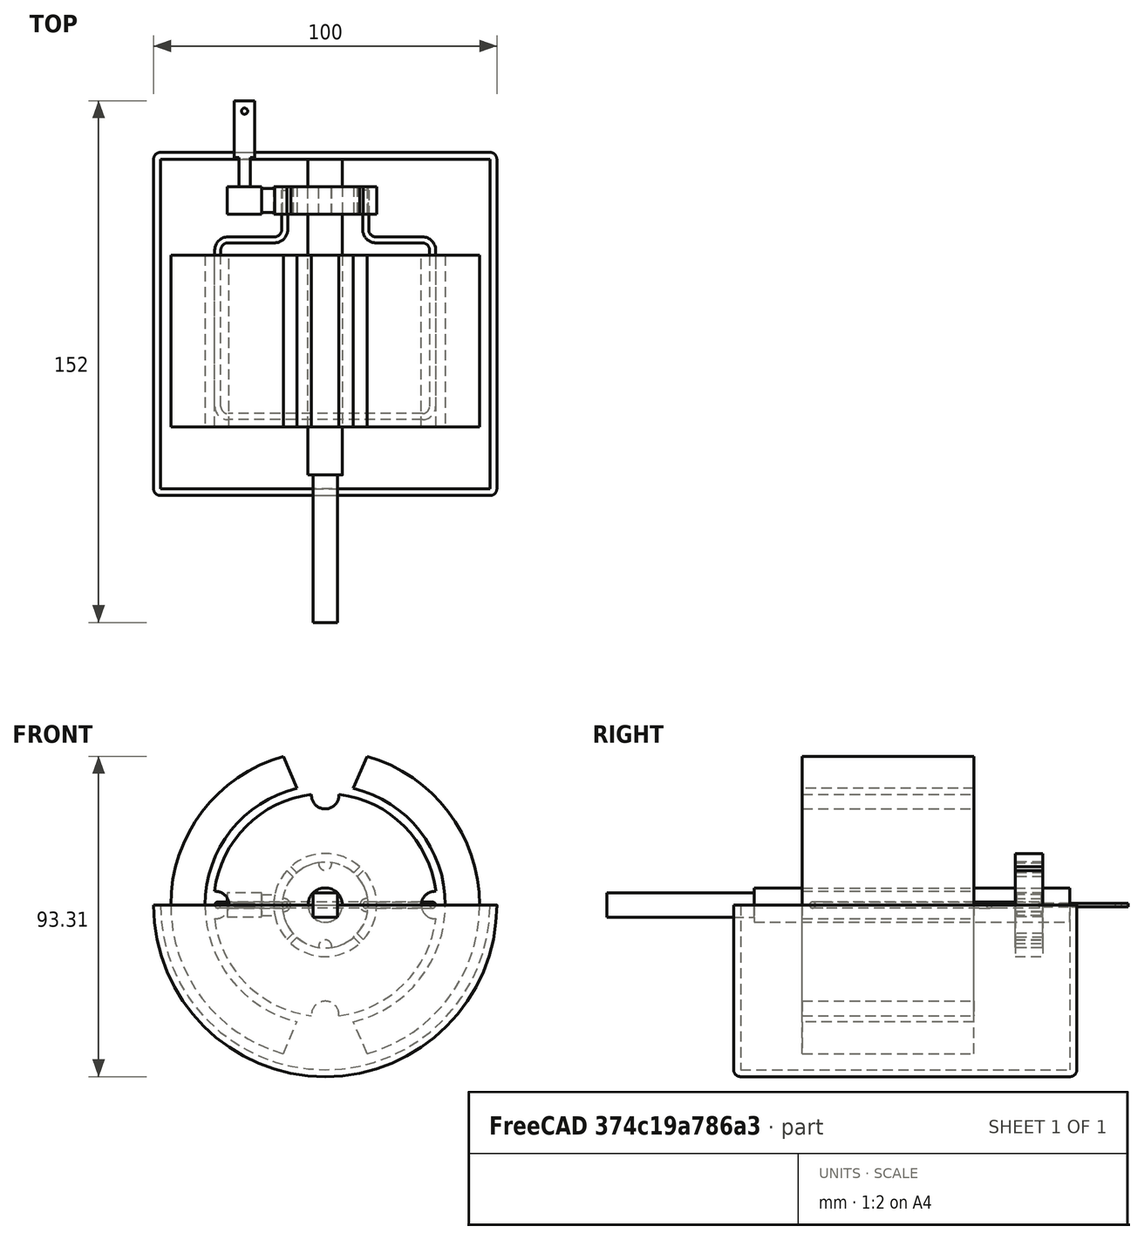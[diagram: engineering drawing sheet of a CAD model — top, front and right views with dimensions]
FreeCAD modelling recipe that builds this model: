
FCSTD DOCUMENT  (FreeCAD 1.0R39285 (Git))
Label: DCmotor
License: All rights reserved
LicenseURL: https://en.wikipedia.org/wiki/All_rights_reserved
objects: Sketcher::SketchObject×28, App::Link×15, PartDesign::Pocket×14, PartDesign::Pad×11, PartDesign::Body×10, PartDesign::Fillet×2, PartDesign::AdditivePipe×1, Spreadsheet::Sheet×1, App::DocumentObjectGroup×1, App::FeaturePython×1, Assembly::JointGroup×1, Assembly::AssemblyObject×1
note: 150 computed .brp shape members not serialized (recipe doc carries the construction recipe); baked Part::Feature solids carry a one-line shape summary decoded from their .brp

FEATURE [Sketcher::SketchObject] Sketch
  ArcFitTolerance = 1e-06
  AttachmentSupport = -> [XZ_Plane]
  FullyConstrained = true
  MakeInternals = false
  MapMode = 5
  Placement = pos=(0,0,0) rot=(1,0,0;1.5708rad)
  sketch-geometry (1):
    g0: Circle CenterX=0 CenterY=0 CenterZ=0 NormalX=0 NormalY=0 NormalZ=1 AngleXU=0 Radius=15
  constraints (2):
    c: Coincident(g0,g-1)
    c: Diameter(g0) = 30
FEATURE [PartDesign::Pad] Pad
  Direction = (0,-1,2e-16)
  Length = 8
  Length2 = 10
  Placement = pos=(0,0,0) rot=(1,0,0;1.5708rad)
  Profile = -> Sketch
  ReferenceAxis = -> Sketch [N_Axis]
  Refine = true
  Suppressed = false
  Type = 0
FEATURE [Sketcher::SketchObject] Sketch001
  ArcFitTolerance = 1e-06
  AttachmentSupport = -> [Pad]
  FullyConstrained = true
  MakeInternals = false
  MapMode = 5
  Placement = pos=(0,-8,0) rot=(1,0,0;1.5708rad)
  sketch-geometry (1):
    g0: Circle CenterX=0 CenterY=0 CenterZ=0 NormalX=0 NormalY=0 NormalZ=1 AngleXU=0 Radius=12.5
  constraints (2):
    c: Diameter(g0) = 25
    c: Coincident(g0,g-1)
FEATURE [PartDesign::Pocket] Pocket
  BaseFeature = -> Pad
  Direction = (0,1,-2e-16)
  Length = 5
  Length2 = 5
  Placement = pos=(0,0,0) rot=(1,0,0;1.5708rad)
  Profile = -> Sketch001
  ReferenceAxis = -> Sketch001 [N_Axis]
  Refine = true
  Suppressed = false
  Type = 1
FEATURE [Sketcher::SketchObject] Sketch002
  ArcFitTolerance = 1e-06
  AttachmentSupport = -> [Pocket]
  ExternalGeometry = -> [Pocket]
  FullyConstrained = true
  MakeInternals = false
  MapMode = 5
  Placement = pos=(0,-8,0) rot=(1,0,0;1.5708rad)
  sketch-geometry (8):
    g0: LineSegment StartX=-0.75 StartY=18.87 StartZ=0 EndX=-0.75 EndY=-18.87 EndZ=0
    g1: LineSegment StartX=-0.75 StartY=-18.87 StartZ=0 EndX=0.75 EndY=-18.87 EndZ=0
    g2: LineSegment StartX=0.75 StartY=-18.87 StartZ=0 EndX=0.75 EndY=18.87 EndZ=0
    g3: LineSegment StartX=0.75 StartY=18.87 StartZ=0 EndX=-0.75 EndY=18.87 EndZ=0
    g4: LineSegment StartX=-17.13 StartY=0.75 StartZ=0 EndX=-17.13 EndY=-0.75 EndZ=0
    g5: LineSegment StartX=-17.13 StartY=-0.75 StartZ=0 EndX=17.73 EndY=-0.75 EndZ=0
    g6: LineSegment StartX=17.73 StartY=-0.75 StartZ=0 EndX=17.73 EndY=0.75 EndZ=0
    g7: LineSegment StartX=17.73 StartY=0.75 StartZ=0 EndX=-17.13 EndY=0.75 EndZ=0
  constraints (21):
    c: Coincident(g0,g1)
    c: Coincident(g1,g2)
    c: Coincident(g2,g3)
    c: Coincident(g3,g0)
    c: Vertical(g0)
    c: Horizontal(g1)
    c: Symmetric(g0,g2,g-2)
    c: DistanceX(g0,g-1) = 0.75
    c: Coincident(g4,g5)
    c: Coincident(g5,g6)
    c: Coincident(g6,g7)
    c: Coincident(g7,g4)
    c: Vertical(g4)
    c: Horizontal(g5)
    c: Horizontal(g7)
    c: Symmetric(g5,g6,g-1)
    c: DistanceY(g5,g-1) = 0.75
    c: Symmetric(g1,g2,g-1)
    c: DistanceY(g1,g-1) = 18.87
    c: DistanceX(g4,g-1) = 17.13
    c: DistanceX(g-1,g5) = 17.73
FEATURE [PartDesign::Pocket] Pocket001
  BaseFeature = -> Pocket
  Direction = (0,1,-2e-16)
  Length = 5
  Length2 = 5
  Placement = pos=(0,0,0) rot=(1,0,0;1.5708rad)
  Profile = -> Sketch002
  ReferenceAxis = -> Sketch002 [N_Axis]
  Refine = true
  Suppressed = false
  Type = 1
FEATURE [PartDesign::Body] Body  label="Commutator"
  AllowCompound = true
  Group = -> [Sketch,Pad,Sketch001,Pocket,Sketch002,Pocket001]
  Origin = -> Origin
  Placement = pos=(0,15,1.08e-14) rot=(0,1,0;0.785398rad)
  Tip = -> Pocket001
FEATURE [Sketcher::SketchObject] Sketch003
  ArcFitTolerance = 1e-06
  AttachmentSupport = -> [XZ_Plane001]
  FullyConstrained = true
  MakeInternals = false
  MapMode = 5
  Placement = pos=(0,0,0) rot=(1,0,0;1.5708rad)
  sketch-geometry (1):
    g0: Circle CenterX=0 CenterY=0 CenterZ=0 NormalX=0 NormalY=0 NormalZ=1 AngleXU=0 Radius=45
  constraints (2):
    c: Coincident(g0,g-1)
    c: Diameter(g0) = 90
FEATURE [PartDesign::Pad] Pad001
  Direction = (0,-1,2e-16)
  Length = 50
  Length2 = 10
  Placement = pos=(0,0,0) rot=(1,0,0;1.5708rad)
  Profile = -> Sketch003
  ReferenceAxis = -> Sketch003 [N_Axis]
  Refine = true
  Suppressed = false
  Type = 0
FEATURE [Sketcher::SketchObject] Sketch004
  ArcFitTolerance = 1e-06
  AttachmentSupport = -> [Pad001]
  FullyConstrained = true
  MakeInternals = false
  MapMode = 5
  Placement = pos=(0,-50,0) rot=(1,0,0;1.5708rad)
  sketch-geometry (1):
    g0: Circle CenterX=0 CenterY=0 CenterZ=0 NormalX=0 NormalY=0 NormalZ=1 AngleXU=0 Radius=35
  constraints (2):
    c: Diameter(g0) = 70
    c: Coincident(g0,g-1)
FEATURE [PartDesign::Pocket] Pocket002
  BaseFeature = -> Pad001
  Direction = (0,1,-2e-16)
  Length = 5
  Length2 = 5
  Placement = pos=(0,0,0) rot=(1,0,0;1.5708rad)
  Profile = -> Sketch004
  ReferenceAxis = -> Sketch004 [N_Axis]
  Refine = true
  Suppressed = false
  Type = 1
FEATURE [Sketcher::SketchObject] Sketch005
  ArcFitTolerance = 1e-06
  AttachmentSupport = -> [Pocket002]
  ExternalGeometry = -> [Pocket002]
  FullyConstrained = true
  MakeInternals = false
  MapMode = 5
  Placement = pos=(0,-50,0) rot=(1,0,0;1.5708rad)
  sketch-geometry (8):
    g0: LineSegment StartX=-13 StartY=45.18 StartZ=0 EndX=13 EndY=45.18 EndZ=0
    g1: LineSegment StartX=-8.2 StartY=34 StartZ=0 EndX=8.2 EndY=34 EndZ=0
    g2: LineSegment StartX=-13 StartY=45.18 StartZ=0 EndX=-8.2 EndY=34 EndZ=0
    g3: LineSegment StartX=8.2 StartY=34 StartZ=0 EndX=13 EndY=45.18 EndZ=0
    g4: LineSegment StartX=-8.2 StartY=-34 StartZ=0 EndX=8.2 EndY=-34 EndZ=0
    g5: LineSegment StartX=8.2 StartY=-34 StartZ=0 EndX=13 EndY=-45.18 EndZ=0
    g6: LineSegment StartX=13 StartY=-45.18 StartZ=0 EndX=-13 EndY=-45.18 EndZ=0
    g7: LineSegment StartX=-13 StartY=-45.18 StartZ=0 EndX=-8.2 EndY=-34 EndZ=0
  constraints (20):
    c: DistanceX(g0,g-1) = 13
    c: Symmetric(g0,g0,g-2)
    c: Symmetric(g1,g1,g-2)
    c: DistanceX(g1,g-1) = 8.2
    c: Coincident(g2,g0)
    c: Coincident(g2,g1)
    c: Coincident(g3,g1)
    c: Coincident(g3,g0)
    c: DistanceY(g-1,g1) = 34
    c: DistanceY(g-1,g0) = 45.18
    c: Coincident(g4,g5)
    c: Coincident(g5,g6)
    c: Coincident(g6,g7)
    c: Coincident(g7,g4)
    c: Vertical(g4,g1)
    c: Symmetric(g4,g4,g-2)
    c: Symmetric(g6,g5,g-2)
    c: Vertical(g6,g0)
    c: Equal(g2,g7)
    c: DistanceY(g4,g-1) = 34
FEATURE [PartDesign::Pocket] Pocket003
  BaseFeature = -> Pocket002
  Direction = (0,1,-2e-16)
  Length = 5
  Length2 = 5
  Placement = pos=(0,0,0) rot=(1,0,0;1.5708rad)
  Profile = -> Sketch005
  ReferenceAxis = -> Sketch005 [N_Axis]
  Refine = true
  Suppressed = false
  Type = 1
FEATURE [PartDesign::Body] Body001  label="NorthMagnet"
  AllowCompound = false
  Group = -> [Sketch003,Pad001,Sketch004,Pocket002,Sketch005,Pocket003]
  Origin = -> Origin001
  Placement = pos=(0,-5,0) rot=(0,0,1;0rad)
  Tip = -> Pocket003
FEATURE [Sketcher::SketchObject] Sketch006
  ArcFitTolerance = 1e-06
  AttachmentSupport = -> [XZ_Plane002]
  FullyConstrained = true
  MakeInternals = false
  MapMode = 5
  Placement = pos=(0,0,0) rot=(1,0,0;1.5708rad)
  sketch-geometry (12):
    g0: LineSegment StartX=-18.57 StartY=3 StartZ=0 EndX=-18.57 EndY=-3 EndZ=0
    g1: LineSegment StartX=-18.57 StartY=-3 StartZ=0 EndX=-13.57 EndY=-3 EndZ=0
    g2: LineSegment StartX=-13.57 StartY=-3 StartZ=0 EndX=-13.57 EndY=3 EndZ=0
    g3: LineSegment StartX=-13.57 StartY=3 StartZ=0 EndX=-18.57 EndY=3 EndZ=0
    g4: LineSegment StartX=-28.57 StartY=3.5 StartZ=0 EndX=-28.57 EndY=-3.5 EndZ=0
    g5: LineSegment StartX=-28.57 StartY=-3.5 StartZ=0 EndX=-18.57 EndY=-3.5 EndZ=0
    g6: LineSegment StartX=-18.57 StartY=-3.5 StartZ=0 EndX=-18.57 EndY=3.5 EndZ=0
    g7: LineSegment StartX=-18.57 StartY=3.5 StartZ=0 EndX=-28.57 EndY=3.5 EndZ=0
    g8: LineSegment StartX=-31.07 StartY=0.75 StartZ=0 EndX=-31.07 EndY=-0.75 EndZ=0
    g9: LineSegment StartX=-31.07 StartY=-0.75 StartZ=0 EndX=-28.57 EndY=-0.75 EndZ=0
    g10: LineSegment StartX=-28.57 StartY=-0.75 StartZ=0 EndX=-28.57 EndY=0.75 EndZ=0
    g11: LineSegment StartX=-28.57 StartY=0.75 StartZ=0 EndX=-31.07 EndY=0.75 EndZ=0
  constraints (33):
    c: Coincident(g0,g1)
    c: Coincident(g1,g2)
    c: Coincident(g2,g3)
    c: Coincident(g3,g0)
    c: Vertical(g0)
    c: Horizontal(g1)
    c: Horizontal(g3)
    c: Symmetric(g1,g2,g-1)
    c: DistanceY(g-1,g2) = 3
    c: DistanceX(g0,g2) = 5
    c: DistanceX(g1,g-1) = 13.57
    c: Coincident(g4,g5)
    c: Coincident(g5,g6)
    c: Coincident(g6,g7)
    c: Coincident(g7,g4)
    c: Vertical(g4)
    c: Horizontal(g5)
    c: Horizontal(g7)
    c: Vertical(g6,g0)
    c: DistanceX(g4,g6) = 10
    c: DistanceY(g4,g4) = 7
    c: Symmetric(g5,g6,g-1)
    c: Coincident(g8,g9)
    c: Coincident(g9,g10)
    c: Coincident(g10,g11)
    c: Coincident(g11,g8)
    c: Vertical(g8)
    c: Horizontal(g9)
    c: Horizontal(g11)
    c: Vertical(g9,g4)
    c: Symmetric(g9,g10,g-1)
    c: DistanceY(g8,g8) = 1.5
    c: DistanceX(g8,g9) = 2.5
FEATURE [PartDesign::Pad] Pad002
  Direction = (0,-1,2e-16)
  Length = 8
  Length2 = 10
  Placement = pos=(0,0,0) rot=(1,0,0;1.5708rad)
  Profile = -> Sketch006
  ReferenceAxis = -> Sketch006 [N_Axis]
  Refine = true
  Suppressed = false
  Type = 0
FEATURE [Sketcher::SketchObject] Sketch007
  ArcFitTolerance = 1e-06
  AttachmentSupport = -> [Pad002]
  FullyConstrained = true
  MakeInternals = false
  MapMode = 5
  Placement = pos=(0,-8,4.2e-15) rot=(1,0,0;1.5708rad)
  sketch-geometry (1):
    g0: Circle CenterX=0 CenterY=0 CenterZ=0 NormalX=0 NormalY=0 NormalZ=1 AngleXU=0 Radius=15
  constraints (2):
    c: Diameter(g0) = 30
    c: Coincident(g0,g-1)
FEATURE [PartDesign::Pocket] Pocket004
  BaseFeature = -> Pad002
  Direction = (0,1,-2e-16)
  Length = 5
  Length2 = 5
  Placement = pos=(0,0,0) rot=(1,0,0;1.5708rad)
  Profile = -> Sketch007
  ReferenceAxis = -> Sketch007 [N_Axis]
  Refine = true
  Suppressed = false
  Type = 1
FEATURE [Sketcher::SketchObject] Sketch008
  ArcFitTolerance = 1e-06
  AttachmentSupport = -> [Pocket004]
  ExternalGeometry = -> [Pocket004]
  FullyConstrained = true
  MakeInternals = false
  MapMode = 5
  Placement = pos=(0,3e-16,0.75) rot=(0,0,1;3.14159rad)
  sketch-geometry (8):
    g0: LineSegment StartX=31.07 StartY=8 StartZ=0 EndX=28.57 EndY=8 EndZ=0
    g1: LineSegment StartX=28.57 StartY=8 StartZ=0 EndX=28.57 EndY=3.51 EndZ=0
    g2: LineSegment StartX=28.57 StartY=3.51 StartZ=0 EndX=31.07 EndY=3.51 EndZ=0
    g3: LineSegment StartX=31.07 StartY=3.51 StartZ=0 EndX=31.07 EndY=8 EndZ=0
    g4: LineSegment StartX=28.57 StartY=4.49 StartZ=0 EndX=28.57 EndY=0 EndZ=0
    g5: LineSegment StartX=28.57 StartY=0 StartZ=0 EndX=31.07 EndY=0 EndZ=0
    g6: LineSegment StartX=31.07 StartY=0 StartZ=0 EndX=31.07 EndY=4.49 EndZ=0
    g7: LineSegment StartX=31.07 StartY=4.49 StartZ=0 EndX=28.57 EndY=4.49 EndZ=0
  constraints (23):
    c: Coincident(g0,g1)
    c: Coincident(g1,g2)
    c: Coincident(g2,g3)
    c: Coincident(g3,g0)
    c: Horizontal(g0)
    c: Horizontal(g2)
    c: Vertical(g1)
    c: Vertical(g3)
    c: Coincident(g0,g-4)
    c: PointOnObject(g1,g-3)
    c: Coincident(g4,g5)
    c: Coincident(g5,g6)
    c: Coincident(g6,g7)
    c: Coincident(g7,g4)
    c: Vertical(g4)
    c: Vertical(g6)
    c: Horizontal(g5)
    c: Horizontal(g7)
    c: PointOnObject(g4,g-3)
    c: PointOnObject(g5,g-1)
    c: Vertical(g6,g2)
    c: Equal(g6,g3)
    c: DistanceY(g-1,g2) = 3.51
FEATURE [PartDesign::Pocket] Pocket005
  BaseFeature = -> Pocket004
  Direction = (0,0,-1)
  Length = 5
  Length2 = 5
  Placement = pos=(0,0,0) rot=(1,0,0;1.5708rad)
  Profile = -> Sketch008
  ReferenceAxis = -> Sketch008 [N_Axis]
  Refine = true
  Suppressed = false
  Type = 1
FEATURE [Sketcher::SketchObject] Sketch009
  ArcFitTolerance = 1e-06
  AttachmentSupport = -> [Pocket005]
  ExternalGeometry = -> [Pocket005]
  FullyConstrained = true
  MakeInternals = false
  MapMode = 5
  Placement = pos=(0,1.3e-15,3) rot=(0,0,1;3.14159rad)
  sketch-geometry (8):
    g0: LineSegment StartX=14.6969 StartY=8 StartZ=0 EndX=14.6969 EndY=7.5 EndZ=0
    g1: LineSegment StartX=14.6969 StartY=7.5 StartZ=0 EndX=18.57 EndY=7.5 EndZ=0
    g2: LineSegment StartX=18.57 StartY=7.5 StartZ=0 EndX=18.57 EndY=8 EndZ=0
    g3: LineSegment StartX=18.57 StartY=8 StartZ=0 EndX=14.6969 EndY=8 EndZ=0
    g4: LineSegment StartX=14.6969 StartY=0.5 StartZ=0 EndX=14.6969 EndY=-1e-16 EndZ=0
    g5: LineSegment StartX=14.6969 StartY=-1e-16 StartZ=0 EndX=18.57 EndY=-1e-16 EndZ=0
    g6: LineSegment StartX=18.57 StartY=-1e-16 StartZ=0 EndX=18.57 EndY=0.5 EndZ=0
    g7: LineSegment StartX=18.57 StartY=0.5 StartZ=0 EndX=14.6969 EndY=0.5 EndZ=0
  constraints (22):
    c: Coincident(g0,g1)
    c: Coincident(g1,g2)
    c: Coincident(g2,g3)
    c: Coincident(g3,g0)
    c: Vertical(g0)
    c: Vertical(g2)
    c: Horizontal(g1)
    c: Horizontal(g3)
    c: Coincident(g0,g-5)
    c: PointOnObject(g1,g-4)
    c: DistanceY(g1,g2) = 0.5
    c: Coincident(g4,g5)
    c: Coincident(g5,g6)
    c: Coincident(g6,g7)
    c: Coincident(g7,g4)
    c: Vertical(g4)
    c: Vertical(g6)
    c: Horizontal(g5)
    c: Horizontal(g7)
    c: PointOnObject(g4,g-5)
    c: Coincident(g5,g-4)
    c: DistanceY(g4,g4) = 0.5
FEATURE [PartDesign::Pocket] Pocket006
  BaseFeature = -> Pocket005
  Direction = (0,0,-1)
  Length = 5
  Length2 = 5
  Placement = pos=(0,0,0) rot=(1,0,0;1.5708rad)
  Profile = -> Sketch009
  ReferenceAxis = -> Sketch009 [N_Axis]
  Refine = true
  Suppressed = false
  Type = 1
FEATURE [PartDesign::Body] Body002  label="Brush"
  AllowCompound = false
  Group = -> [Sketch006,Pad002,Sketch007,Pocket004,Sketch008,Pocket005,Sketch009,Pocket006]
  Origin = -> Origin002
  Placement = pos=(0,15,0) rot=(0,0,1;0rad)
  Tip = -> Pocket006
FEATURE [Sketcher::SketchObject] Sketch010
  ArcFitTolerance = 1e-06
  AttachmentSupport = -> [XZ_Plane003]
  FullyConstrained = true
  MakeInternals = false
  MapMode = 5
  Placement = pos=(0,0,0) rot=(1,0,0;1.5708rad)
  sketch-geometry (1):
    g0: Circle CenterX=0 CenterY=0 CenterZ=0 NormalX=0 NormalY=0 NormalZ=1 AngleXU=0 Radius=45
  constraints (2):
    c: Coincident(g0,g-1)
    c: Diameter(g0) = 90
FEATURE [PartDesign::Pad] Pad003
  Direction = (0,-1,2e-16)
  Length = 50
  Length2 = 10
  Placement = pos=(0,0,0) rot=(1,0,0;1.5708rad)
  Profile = -> Sketch010
  ReferenceAxis = -> Sketch010 [N_Axis]
  Refine = true
  Suppressed = false
  Type = 0
FEATURE [Sketcher::SketchObject] Sketch011
  ArcFitTolerance = 1e-06
  AttachmentSupport = -> [Pad003]
  FullyConstrained = true
  MakeInternals = false
  MapMode = 5
  Placement = pos=(0,-50,0) rot=(1,0,0;1.5708rad)
  sketch-geometry (1):
    g0: Circle CenterX=0 CenterY=0 CenterZ=0 NormalX=0 NormalY=0 NormalZ=1 AngleXU=0 Radius=35
  constraints (2):
    c: Diameter(g0) = 70
    c: Coincident(g0,g-1)
FEATURE [PartDesign::Pocket] Pocket007
  BaseFeature = -> Pad003
  Direction = (0,1,-2e-16)
  Length = 5
  Length2 = 5
  Placement = pos=(0,0,0) rot=(1,0,0;1.5708rad)
  Profile = -> Sketch011
  ReferenceAxis = -> Sketch011 [N_Axis]
  Refine = true
  Suppressed = false
  Type = 1
FEATURE [Sketcher::SketchObject] Sketch012
  ArcFitTolerance = 1e-06
  AttachmentSupport = -> [Pocket007]
  ExternalGeometry = -> [Pocket007]
  FullyConstrained = true
  MakeInternals = false
  MapMode = 5
  Placement = pos=(0,-50,0) rot=(1,0,0;1.5708rad)
  sketch-geometry (8):
    g0: LineSegment StartX=-13 StartY=45.18 StartZ=0 EndX=13 EndY=45.18 EndZ=0
    g1: LineSegment StartX=-8.2 StartY=34 StartZ=0 EndX=8.2 EndY=34 EndZ=0
    g2: LineSegment StartX=-13 StartY=45.18 StartZ=0 EndX=-8.2 EndY=34 EndZ=0
    g3: LineSegment StartX=8.2 StartY=34 StartZ=0 EndX=13 EndY=45.18 EndZ=0
    g4: LineSegment StartX=-8.2 StartY=-34 StartZ=0 EndX=8.2 EndY=-34 EndZ=0
    g5: LineSegment StartX=8.2 StartY=-34 StartZ=0 EndX=13 EndY=-45.18 EndZ=0
    g6: LineSegment StartX=13 StartY=-45.18 StartZ=0 EndX=-13 EndY=-45.18 EndZ=0
    g7: LineSegment StartX=-13 StartY=-45.18 StartZ=0 EndX=-8.2 EndY=-34 EndZ=0
  constraints (20):
    c: DistanceX(g0,g-1) = 13
    c: Symmetric(g0,g0,g-2)
    c: Symmetric(g1,g1,g-2)
    c: DistanceX(g1,g-1) = 8.2
    c: Coincident(g2,g0)
    c: Coincident(g2,g1)
    c: Coincident(g3,g1)
    c: Coincident(g3,g0)
    c: DistanceY(g-1,g1) = 34
    c: DistanceY(g-1,g0) = 45.18
    c: Coincident(g4,g5)
    c: Coincident(g5,g6)
    c: Coincident(g6,g7)
    c: Coincident(g7,g4)
    c: Vertical(g4,g1)
    c: Symmetric(g4,g4,g-2)
    c: Symmetric(g6,g5,g-2)
    c: Vertical(g6,g0)
    c: Equal(g2,g7)
    c: DistanceY(g4,g-1) = 34
FEATURE [PartDesign::Pocket] Pocket008
  BaseFeature = -> Pocket007
  Direction = (0,1,-2e-16)
  Length = 5
  Length2 = 5
  Placement = pos=(0,0,0) rot=(1,0,0;1.5708rad)
  Profile = -> Sketch012
  ReferenceAxis = -> Sketch012 [N_Axis]
  Refine = true
  Suppressed = false
  Type = 1
FEATURE [PartDesign::Body] Body003  label="SouthMagnet"
  AllowCompound = false
  Group = -> [Sketch010,Pad003,Sketch011,Pocket007,Sketch012,Pocket008]
  Origin = -> Origin003
  Placement = pos=(0,-5,0) rot=(0,1,0;3.14159rad)
  Tip = -> Pocket008
FEATURE [Sketcher::SketchObject] Sketch013
  ArcFitTolerance = 1e-06
  AttachmentSupport = -> [XY_Plane004]
  FullyConstrained = true
  MakeInternals = false
  MapMode = 5
  sketch-geometry (19):
    g0: LineSegment StartX=11.8 StartY=11 StartZ=0 EndX=11.8 EndY=-0.5 EndZ=0
    g1: LineSegment StartX=14.8 StartY=-3.5 StartZ=0 EndX=28.3 EndY=-3.5 EndZ=0
    g2: LineSegment StartX=31.3 StartY=-6.5 StartZ=0 EndX=31.3 EndY=-52 EndZ=0
    g3: LineSegment StartX=28.3 StartY=-55 StartZ=0 EndX=-28.3 EndY=-55 EndZ=0
    g4: LineSegment StartX=-31.3 StartY=-52 StartZ=0 EndX=-31.3 EndY=-6.5 EndZ=0
    g5: LineSegment StartX=-28.3 StartY=-3.5 StartZ=0 EndX=-14.8 EndY=-3.5 EndZ=0
    g6: LineSegment StartX=-11.8 StartY=-0.5 StartZ=0 EndX=-11.8 EndY=11 EndZ=0
    g7: ArcOfCircle CenterX=28.3 CenterY=-6.5 CenterZ=0 NormalX=0 NormalY=0 NormalZ=1 AngleXU=0 Radius=3 StartAngle=0 EndAngle=1.5708
    g8: GeomPoint [constr] X=31.3 Y=-3.5 Z=0
    g9: ArcOfCircle CenterX=28.3 CenterY=-52 CenterZ=0 NormalX=0 NormalY=0 NormalZ=1 AngleXU=0 Radius=3 StartAngle=4.71239 EndAngle=6.28319
    g10: GeomPoint [constr] X=31.3 Y=-55 Z=0
    g11: ArcOfCircle CenterX=-28.3 CenterY=-6.5 CenterZ=0 NormalX=0 NormalY=0 NormalZ=1 AngleXU=0 Radius=3 StartAngle=1.5708 EndAngle=3.14159
    g12: GeomPoint [constr] X=-31.3 Y=-3.5 Z=0
    g13: ArcOfCircle CenterX=-28.3 CenterY=-52 CenterZ=0 NormalX=0 NormalY=0 NormalZ=1 AngleXU=0 Radius=3 StartAngle=3.14159 EndAngle=4.71239
    g14: GeomPoint [constr] X=-31.3 Y=-55 Z=0
    g15: ArcOfCircle CenterX=14.8 CenterY=-0.5 CenterZ=0 NormalX=0 NormalY=0 NormalZ=1 AngleXU=0 Radius=3 StartAngle=3.14159 EndAngle=4.71239
    g16: GeomPoint [constr] X=11.8 Y=-3.5 Z=0
    g17: ArcOfCircle CenterX=-14.8 CenterY=-0.5 CenterZ=0 NormalX=0 NormalY=0 NormalZ=1 AngleXU=0 Radius=3 StartAngle=4.71239 EndAngle=6.28319
    g18: GeomPoint [constr] X=-11.8 Y=-3.5 Z=0
  constraints (44):
    c: Vertical(g0)
    c: Horizontal(g1)
    c: Vertical(g2)
    c: Vertical(g4)
    c: Horizontal(g5)
    c: Vertical(g6)
    c: Symmetric(g6,g0,g-2)
    c: Horizontal(g16,g18)
    c: Symmetric(g10,g14,g-2)
    c: DistanceX(g6,g-1) = 11.8
    c: DistanceY(g-1,g6) = 11
    c: DistanceX(g12,g18) = 19.5
    c: DistanceY(g12,g-1) = 3.5
    c: DistanceY(g14,g-1) = 55
    c: PointOnObject(g8,g1)
    c: PointOnObject(g8,g2)
    c: Tangent(g1,g7) = 1.5708
    c: Tangent(g2,g7) = 1.5708
    c: DistanceX(g7,g2) = 3
    c: PointOnObject(g10,g2)
    c: PointOnObject(g10,g3)
    c: Tangent(g2,g9) = 1.5708
    c: Tangent(g3,g9) = 1.5708
    c: PointOnObject(g12,g4)
    c: PointOnObject(g12,g5)
    c: Tangent(g4,g11) = 1.5708
    c: Tangent(g5,g11) = 1.5708
    c: PointOnObject(g14,g3)
    c: PointOnObject(g14,g4)
    c: Tangent(g3,g13) = 1.5708
    c: Tangent(g4,g13) = 1.5708
    c: Vertical(g1,g3)
    c: Horizontal(g2,g4)
    c: Vertical(g3,g5)
    c: PointOnObject(g16,g0)
    c: PointOnObject(g16,g1)
    c: Tangent(g0,g15) = -1.5708
    c: Tangent(g1,g15) = -1.5708
    c: PointOnObject(g18,g5)
    c: PointOnObject(g18,g6)
    c: Tangent(g5,g17) = -1.5708
    c: Tangent(g6,g17) = -1.5708
    c: Equal(g11,g17)
    c: Equal(g17,g15)
FEATURE [Sketcher::SketchObject] Sketch014
  ArcFitTolerance = 1e-06
  AttachmentSupport = -> [XZ_Plane004]
  FullyConstrained = true
  MakeInternals = false
  MapMode = 5
  Placement = pos=(0,0,0) rot=(1,0,0;1.5708rad)
  sketch-geometry (1):
    g0: Circle CenterX=11.8 CenterY=0 CenterZ=0 NormalX=0 NormalY=0 NormalZ=1 AngleXU=0 Radius=0.875
  constraints (3):
    c: Diameter(g0) = 1.75
    c: PointOnObject(g0,g-1)
    c: DistanceX(g-1,g0) = 11.8
FEATURE [PartDesign::AdditivePipe] AdditivePipe
  AuxilleryCurvelinear = true
  AuxillerySpineTangent = false
  Binormal = (0,0,0)
  Mode = 0
  Placement = pos=(0,0,0) rot=(1,0,0;1.5708rad)
  Profile = -> Sketch014
  Refine = true
  Spine = -> Sketch013
  SpineTangent = false
  Suppressed = false
  Transformation = 0
  Transition = 0
FEATURE [PartDesign::Body] Body004  label="Rotor"
  AllowCompound = false
  Group = -> [Sketch013,Sketch014,AdditivePipe]
  Origin = -> Origin004
  Placement = pos=(0,3,0) rot=(0,1,0;0rad)
  Tip = -> AdditivePipe
FEATURE [Sketcher::SketchObject] Sketch015
  ArcFitTolerance = 1e-06
  AttachmentSupport = -> [XZ_Plane006]
  FullyConstrained = true
  MakeInternals = false
  MapMode = 5
  Placement = pos=(0,0,0) rot=(1,0,0;1.5708rad)
  sketch-geometry (1):
    g0: Circle CenterX=0 CenterY=0 CenterZ=0 NormalX=0 NormalY=0 NormalZ=1 AngleXU=0 Radius=5
  constraints (2):
    c: Coincident(g0,g-1)
    c: Diameter(g0) = 10
FEATURE [PartDesign::Pad] Pad004
  Direction = (0,-1,2e-16)
  Length = 135
  Length2 = 10
  Placement = pos=(0,0,0) rot=(1,0,0;1.5708rad)
  Profile = -> Sketch015 [Edge1]
  ReferenceAxis = -> Sketch015 [N_Axis]
  Refine = true
  Suppressed = false
  Type = 0
FEATURE [Sketcher::SketchObject] Sketch016
  ArcFitTolerance = 1e-06
  AttachmentSupport = -> [XY_Plane007]
  FullyConstrained = true
  MakeInternals = false
  MapMode = 5
  sketch-geometry (9):
    g0: LineSegment StartX=-25.16 StartY=15 StartZ=0 EndX=-25.16 EndY=23.5 EndZ=0
    g1: LineSegment StartX=-25.16 StartY=23.5 StartZ=0 EndX=-26.49 EndY=23.5 EndZ=0
    g2: LineSegment StartX=-26.49 StartY=23.5 StartZ=0 EndX=-26.49 EndY=40 EndZ=0
    g3: LineSegment StartX=-26.49 StartY=40 StartZ=0 EndX=-20.5 EndY=40 EndZ=0
    g4: LineSegment StartX=-20.5 StartY=40 StartZ=0 EndX=-20.5 EndY=23.5 EndZ=0
    g5: LineSegment StartX=-20.5 StartY=23.5 StartZ=0 EndX=-21.83 EndY=23.5 EndZ=0
    g6: LineSegment StartX=-21.83 StartY=23.5 StartZ=0 EndX=-21.83 EndY=15 EndZ=0
    g7: LineSegment StartX=-21.83 StartY=15 StartZ=0 EndX=-25.16 EndY=15 EndZ=0
    g8: Circle CenterX=-23.5 CenterY=37 CenterZ=0 NormalX=0 NormalY=0 NormalZ=1 AngleXU=0 Radius=0.9
  constraints (27):
    c: Vertical(g0)
    c: Coincident(g0,g1)
    c: Coincident(g1,g2)
    c: Vertical(g2)
    c: Coincident(g2,g3)
    c: Horizontal(g3)
    c: Coincident(g3,g4)
    c: Vertical(g4)
    c: Coincident(g4,g5)
    c: Horizontal(g5)
    c: Coincident(g5,g6)
    c: Vertical(g6)
    c: Coincident(g6,g7)
    c: Coincident(g7,g0)
    c: Horizontal(g7)
    c: DistanceY(g-1,g0) = 15
    c: Horizontal(g1,g0)
    c: Horizontal(g5,g0)
    c: DistanceX(g6,g-1) = 21.83
    c: DistanceX(g0,g-1) = 25.16
    c: DistanceX(g4,g-1) = 20.5
    c: Equal(g5,g1)
    c: DistanceY(g-1,g4) = 23.5
    c: DistanceY(g-1,g2) = 40
    c: DistanceX(g8,g-1) = 23.5
    c: Diameter(g8) = 1.8
    c: DistanceY(g-1,g8) = 37
FEATURE [PartDesign::Pad] Pad005
  Direction = (0,0,1)
  Length = 1
  Length2 = 10
  Profile = -> Sketch016
  ReferenceAxis = -> Sketch016 [N_Axis]
  Refine = true
  Suppressed = false
  Type = 0
FEATURE [PartDesign::Body] Body006  label="BrushArms"
  AllowCompound = false
  Group = -> [Sketch016,Pad005]
  Origin = -> Origin007
  Placement = pos=(0,0,-0.5) rot=(0,0,1;0rad)
  Tip = -> Pad005
FEATURE [Sketcher::SketchObject] Sketch017
  ArcFitTolerance = 1e-06
  AttachmentSupport = -> [XZ_Plane008]
  FullyConstrained = true
  MakeInternals = false
  MapMode = 5
  Placement = pos=(0,0,0) rot=(1,0,0;1.5708rad)
  sketch-geometry (1):
    g0: Circle CenterX=0 CenterY=0 CenterZ=0 NormalX=0 NormalY=0 NormalZ=1 AngleXU=0 Radius=12.5
  constraints (2):
    c: Diameter(g0) = 25
    c: Coincident(g0,g-1)
FEATURE [PartDesign::Pad] Pad006
  Direction = (0,-1,2e-16)
  Length = 8
  Length2 = 10
  Placement = pos=(0,0,0) rot=(1,0,0;1.5708rad)
  Profile = -> Sketch017
  ReferenceAxis = -> Sketch017 [N_Axis]
  Refine = true
  Suppressed = false
  Type = 0
FEATURE [Sketcher::SketchObject] Sketch018
  ArcFitTolerance = 1e-06
  AttachmentSupport = -> [XZ_Plane008]
  FullyConstrained = true
  MakeInternals = false
  MapMode = 5
  Placement = pos=(0,0,0) rot=(1,0,0;1.5708rad)
  sketch-geometry (4):
    g0: Circle CenterX=12 CenterY=0 CenterZ=0 NormalX=0 NormalY=0 NormalZ=1 AngleXU=0 Radius=1.875
    g1: Circle CenterX=-12 CenterY=0 CenterZ=0 NormalX=0 NormalY=0 NormalZ=1 AngleXU=0 Radius=1.875
    g2: Circle CenterX=0 CenterY=12 CenterZ=0 NormalX=0 NormalY=0 NormalZ=1 AngleXU=0 Radius=1.875
    g3: Circle CenterX=0 CenterY=-12 CenterZ=0 NormalX=0 NormalY=0 NormalZ=1 AngleXU=0 Radius=1.875
  constraints (10):
    c: Diameter(g0) = 3.75
    c: PointOnObject(g0,g-1)
    c: DistanceX(g-1,g0) = 12
    c: Symmetric(g1,g0,g-2)
    c: Equal(g1,g0)
    c: PointOnObject(g2,g-2)
    c: Equal(g2,g1)
    c: DistanceY(g-1,g2) = 12
    c: Equal(g3,g1)
    c: Symmetric(g3,g2,g-1)
FEATURE [PartDesign::Pocket] Pocket009
  BaseFeature = -> Pad006
  Direction = (0,1,-2e-16)
  Length = 5
  Length2 = 5
  Placement = pos=(0,0,0) rot=(1,0,0;1.5708rad)
  Profile = -> Sketch018
  ReferenceAxis = -> Sketch018 [N_Axis]
  Refine = true
  Reversed = true
  Suppressed = false
  Type = 1
FEATURE [PartDesign::Body] Body007  label="CommutatorSupport"
  AllowCompound = false
  Group = -> [Sketch017,Pad006,Sketch018,Pocket009]
  Origin = -> Origin008
  Placement = pos=(0,15,0) rot=(0,1,0;0rad)
  Tip = -> Pocket009
FEATURE [Sketcher::SketchObject] Sketch019
  ArcFitTolerance = 1e-06
  AttachmentSupport = -> [XZ_Plane009]
  FullyConstrained = true
  MakeInternals = false
  MapMode = 5
  Placement = pos=(0,0,0) rot=(1,0,0;1.5708rad)
  sketch-geometry (1):
    g0: Circle CenterX=0 CenterY=0 CenterZ=0 NormalX=0 NormalY=0 NormalZ=1 AngleXU=0 Radius=32.5
  constraints (2):
    c: Diameter(g0) = 65
    c: Coincident(g0,g-1)
FEATURE [PartDesign::Pad] Pad007
  Direction = (0,-1,2e-16)
  Length = 50
  Length2 = 10
  Placement = pos=(0,0,0) rot=(1,0,0;1.5708rad)
  Profile = -> Sketch019
  ReferenceAxis = -> Sketch019 [N_Axis]
  Refine = true
  Suppressed = false
  Type = 0
FEATURE [Sketcher::SketchObject] Sketch020
  ArcFitTolerance = 1e-06
  AttachmentSupport = -> [Pad007]
  FullyConstrained = true
  MakeInternals = false
  MapMode = 5
  Placement = pos=(0,0,0) rot=(-1,0,0;1.5708rad)
  sketch-geometry (4):
    g0: Circle CenterX=32 CenterY=0 CenterZ=0 NormalX=0 NormalY=0 NormalZ=1 AngleXU=0 Radius=4
    g1: Circle CenterX=-32 CenterY=0 CenterZ=0 NormalX=0 NormalY=0 NormalZ=1 AngleXU=0 Radius=4
    g2: Circle CenterX=0 CenterY=-32 CenterZ=0 NormalX=0 NormalY=0 NormalZ=1 AngleXU=0 Radius=4
    g3: Circle CenterX=-2e-16 CenterY=32 CenterZ=0 NormalX=0 NormalY=0 NormalZ=1 AngleXU=0 Radius=4
  constraints (10):
    c: PointOnObject(g0,g-1)
    c: Diameter(g0) = 8
    c: DistanceX(g-1,g0) = 32
    c: Symmetric(g1,g0,g-2)
    c: Equal(g1,g0)
    c: PointOnObject(g2,g-2)
    c: DistanceY(g2,g-1) = 32
    c: Symmetric(g3,g2,g-1)
    c: Equal(g0,g2)
    c: Equal(g3,g0)
FEATURE [PartDesign::Pocket] Pocket010
  BaseFeature = -> Pad007
  Direction = (0,-1,-2e-16)
  Length = 5
  Length2 = 5
  Placement = pos=(0,0,0) rot=(1,0,0;1.5708rad)
  Profile = -> Sketch020
  ReferenceAxis = -> Sketch020 [N_Axis]
  Refine = true
  Suppressed = false
  Type = 1
FEATURE [PartDesign::Body] Body008  label="RotorSupport"
  AllowCompound = false
  Group = -> [Sketch019,Pad007,Sketch020,Pocket010]
  Origin = -> Origin009
  Placement = pos=(0,-5,0) rot=(0,1,0;0rad)
  Tip = -> Pocket010
FEATURE [Sketcher::SketchObject] Sketch021
  ArcFitTolerance = 1e-06
  AttachmentSupport = -> [XZ_Plane010]
  FullyConstrained = true
  MakeInternals = false
  MapMode = 5
  Placement = pos=(0,0,0) rot=(1,0,0;1.5708rad)
  sketch-geometry (2):
    g0: ArcOfCircle CenterX=0 CenterY=0 CenterZ=0 NormalX=0 NormalY=0 NormalZ=1 AngleXU=0 Radius=50 StartAngle=3.14159 EndAngle=6.28319
    g1: LineSegment StartX=50 StartY=-1.22e-14 StartZ=0 EndX=-50 EndY=1.73205e-05 EndZ=0
  constraints (6):
    c: Angle(g0) = 3.14159
    c: Coincident(g0,g-1)
    c: PointOnObject(g0,g-1)
    c: DistanceX(g-1,g0) = 50
    c: Coincident(g1,g0)
    c: Coincident(g1,g0)
FEATURE [PartDesign::Pad] Pad008
  Direction = (0,-1,2e-16)
  Length = 100
  Length2 = 10
  Placement = pos=(0,0,0) rot=(1,0,0;1.5708rad)
  Profile = -> Sketch021
  ReferenceAxis = -> Sketch021 [N_Axis]
  Refine = true
  Suppressed = false
  Type = 0
FEATURE [Sketcher::SketchObject] Sketch022
  ArcFitTolerance = 1e-06
  AttachmentSupport = -> [XZ_Plane010]
  FullyConstrained = true
  MakeInternals = false
  MapMode = 5
  Placement = pos=(0,0,0) rot=(1,0,0;1.5708rad)
  sketch-geometry (2):
    g0: ArcOfCircle CenterX=0 CenterY=0 CenterZ=0 NormalX=0 NormalY=0 NormalZ=1 AngleXU=0 Radius=48 StartAngle=3.14159 EndAngle=6.28319
    g1: LineSegment StartX=48 StartY=0 StartZ=0 EndX=-48 EndY=5.9e-15 EndZ=0
  constraints (6):
    c: Radius(g0) = 48
    c: Coincident(g0,g-1)
    c: PointOnObject(g0,g-1)
    c: PointOnObject(g0,g-1)
    c: Coincident(g1,g0)
    c: Coincident(g1,g0)
FEATURE [PartDesign::Pocket] Pocket011
  BaseFeature = -> Pad008
  Direction = (0,1,-2e-16)
  Length = 5
  Length2 = 5
  Placement = pos=(0,0,0) rot=(1,0,0;1.5708rad)
  Profile = -> Sketch022
  ReferenceAxis = -> Sketch022 [N_Axis]
  Refine = true
  Reversed = true
  Suppressed = false
  Type = 1
FEATURE [Sketcher::SketchObject] Sketch023
  ArcFitTolerance = 1e-06
  AttachmentSupport = -> [XZ_Plane010]
  FullyConstrained = true
  MakeInternals = false
  MapMode = 5
  Placement = pos=(0,0,0) rot=(1,0,0;1.5708rad)
  sketch-geometry (2):
    g0: ArcOfCircle CenterX=0 CenterY=0 CenterZ=0 NormalX=0 NormalY=0 NormalZ=1 AngleXU=0 Radius=48.02 StartAngle=3.14159 EndAngle=6.28319
    g1: LineSegment StartX=-48.02 StartY=0 StartZ=0 EndX=48.02 EndY=0 EndZ=0
  constraints (6):
    c: Radius(g0) = 48.02
    c: Coincident(g0,g-1)
    c: PointOnObject(g0,g-1)
    c: PointOnObject(g0,g-1)
    c: Coincident(g1,g0)
    c: Coincident(g1,g0)
FEATURE [PartDesign::Pad] Pad009
  BaseFeature = -> Pocket011
  Direction = (0,-1,2e-16)
  Length = 2
  Length2 = 10
  Placement = pos=(0,0,0) rot=(1,0,0;1.5708rad)
  Profile = -> Sketch023
  ReferenceAxis = -> Sketch023 [N_Axis]
  Refine = true
  Suppressed = false
  Type = 0
FEATURE [Sketcher::SketchObject] Sketch024
  ArcFitTolerance = 1e-06
  AttachmentSupport = -> [Pad009]
  FullyConstrained = true
  MakeInternals = false
  MapMode = 5
  Placement = pos=(0,-100,2.2e-14) rot=(1,0,0;1.5708rad)
  sketch-geometry (2):
    g0: ArcOfCircle CenterX=0 CenterY=0 CenterZ=0 NormalX=0 NormalY=0 NormalZ=1 AngleXU=0 Radius=48.02 StartAngle=3.14159 EndAngle=6.28319
    g1: LineSegment StartX=-48.02 StartY=5.9e-15 StartZ=0 EndX=48.02 EndY=0 EndZ=0
  constraints (6):
    c: Radius(g0) = 48.02
    c: Coincident(g0,g-1)
    c: PointOnObject(g0,g-1)
    c: PointOnObject(g0,g-1)
    c: Coincident(g1,g0)
    c: Coincident(g1,g0)
FEATURE [PartDesign::Pad] Pad010
  BaseFeature = -> Pad009
  Direction = (0,-1,2e-16)
  Length = 2
  Length2 = 10
  Placement = pos=(0,0,0) rot=(1,0,0;1.5708rad)
  Profile = -> Sketch024
  ReferenceAxis = -> Sketch024 [N_Axis]
  Refine = true
  Reversed = true
  Suppressed = false
  Type = 0
FEATURE [PartDesign::Fillet] Fillet
  Base = -> Pad010 [Edge8]
  BaseFeature = -> Pad010
  Placement = pos=(0,0,0) rot=(1,0,0;1.5708rad)
  Radius = 2
  Refine = true
  SupportTransform = false
  Suppressed = false
  UseAllEdges = false
FEATURE [PartDesign::Fillet] Fillet001
  Base = -> Fillet [Edge3]
  BaseFeature = -> Fillet
  Placement = pos=(0,0,0) rot=(1,0,0;1.5708rad)
  Radius = 2
  Refine = true
  SupportTransform = false
  Suppressed = false
  UseAllEdges = false
FEATURE [Sketcher::SketchObject] Sketch025
  ArcFitTolerance = 1e-06
  AttachmentSupport = -> [XZ_Plane010]
  FullyConstrained = true
  MakeInternals = false
  MapMode = 5
  Placement = pos=(0,0,0) rot=(1,0,0;1.5708rad)
FEATURE [PartDesign::Body] Body009  label="Case"
  AllowCompound = false
  Group = -> [Sketch021,Pad008,Sketch022,Pocket011,Sketch023,Pad009,Sketch024,Pad010,Fillet,Fillet001,Sketch025]
  Origin = -> Origin010
  Placement = pos=(0,25,0) rot=(0,0,1;0rad)
  Tip = -> Fillet001
FEATURE [Sketcher::SketchObject] Sketch026
  ArcFitTolerance = 1e-06
  AttachmentSupport = -> [Pad004]
  ExternalGeometry = -> [Pad004]
  FullyConstrained = true
  MakeInternals = false
  MapMode = 5
  Placement = pos=(0,-135,0) rot=(1,0,0;1.5708rad)
  sketch-geometry (6):
    g0: LineSegment StartX=3.53106 StartY=-3.54 StartZ=0 EndX=3.53106 EndY=3.54 EndZ=0
    g1: LineSegment StartX=3.53106 StartY=3.54 StartZ=0 EndX=-3.53106 EndY=3.54 EndZ=0
    g2: LineSegment StartX=-3.53106 StartY=3.54 StartZ=0 EndX=-3.87 EndY=6.02 EndZ=0
    g3: LineSegment StartX=-3.87 StartY=6.02 StartZ=0 EndX=6.78 EndY=6.02 EndZ=0
    g4: LineSegment StartX=6.78 StartY=6.02 StartZ=0 EndX=6.88 EndY=-3.72 EndZ=0
    g5: LineSegment StartX=6.88 StartY=-3.72 StartZ=0 EndX=3.53106 EndY=-3.54 EndZ=0
  constraints (18):
    c: Coincident(g0,g1)
    c: Vertical(g0)
    c: Horizontal(g1)
    c: PointOnObject(g1,g-3)
    c: PointOnObject(g0,g-3)
    c: Coincident(g1,g2)
    c: Coincident(g2,g3)
    c: Horizontal(g3)
    c: Coincident(g3,g4)
    c: Coincident(g4,g5)
    c: Coincident(g5,g0)
    c: DistanceY(g1,g2) = 2.48
    c: DistanceX(g2,g3) = 10.65
    c: DistanceY(g4,g3) = 9.74
    c: DistanceY(g4,g-1) = 3.72
    c: DistanceX(g-1,g3) = 6.78
    c: PointOnObject(g0,g-3)
    c: DistanceX(g-1,g4) = 6.88
FEATURE [PartDesign::Pocket] Pocket012
  BaseFeature = -> Pad004
  Direction = (0,1,-2e-16)
  Length = 43
  Length2 = 5
  Placement = pos=(0,0,0) rot=(1,0,0;1.5708rad)
  Profile = -> Sketch026
  ReferenceAxis = -> Sketch026 [N_Axis]
  Refine = true
  Suppressed = false
  Type = 0
FEATURE [Sketcher::SketchObject] Sketch027
  ArcFitTolerance = 1e-06
  AttachmentSupport = -> [Pocket012]
  ExternalGeometry = -> [Pocket012]
  FullyConstrained = true
  MakeInternals = false
  MapMode = 5
  Placement = pos=(0,-135,0) rot=(1,0,0;1.5708rad)
  sketch-geometry (6):
    g0: LineSegment StartX=-3.53106 StartY=3.54 StartZ=0 EndX=-3.53106 EndY=-3.54 EndZ=0
    g1: LineSegment StartX=-3.53106 StartY=-3.54 StartZ=0 EndX=3.53106 EndY=-3.54 EndZ=0
    g2: LineSegment StartX=-3.53106 StartY=3.54 StartZ=0 EndX=-6.79 EndY=3.54 EndZ=0
    g3: LineSegment StartX=-6.79 StartY=3.54 StartZ=0 EndX=-6.79 EndY=-6.25 EndZ=0
    g4: LineSegment StartX=-6.79 StartY=-6.25 StartZ=0 EndX=3.53106 EndY=-6.25 EndZ=0
    g5: LineSegment StartX=3.53106 StartY=-6.25 StartZ=0 EndX=3.53106 EndY=-3.54 EndZ=0
  constraints (16):
    c: Coincident(g-5,g0)
    c: PointOnObject(g0,g-3)
    c: Vertical(g0)
    c: Coincident(g0,g1)
    c: Coincident(g1,g-4)
    c: Coincident(g0,g2)
    c: Horizontal(g2)
    c: Coincident(g2,g3)
    c: Coincident(g3,g4)
    c: Horizontal(g4)
    c: Coincident(g4,g5)
    c: Coincident(g5,g1)
    c: Distance(g2,g-2) = 6.79
    c: Vertical(g3,g2)
    c: Vertical(g1,g4)
    c: DistanceY(g3,g-1) = 6.25
FEATURE [PartDesign::Pocket] Pocket013
  BaseFeature = -> Pocket012
  Direction = (0,1,-2e-16)
  Length = 43
  Length2 = 5
  Placement = pos=(0,0,0) rot=(1,0,0;1.5708rad)
  Profile = -> Sketch027
  ReferenceAxis = -> Sketch027 [N_Axis]
  Refine = true
  Suppressed = false
  Type = 0
FEATURE [PartDesign::Body] Body005  label="Shaft"
  AllowCompound = false
  Group = -> [Sketch015,Pad004,Sketch026,Pocket012,Sketch027,Pocket013]
  Origin = -> Origin006
  Placement = pos=(0,23,0) rot=(0,1,0;0rad)
  Tip = -> Pocket013
FEATURE [Spreadsheet::Sheet] Spreadsheet  label="MotorSpreadsheet"
  cells = A1(Angle)=0
FEATURE [App::DocumentObjectGroup] Parts
  Group = -> [Body,Body001,Body002,Body003,Body004,Body005,Body006,Body007,Body008,Body009]
FEATURE [App::Link] Shaft  label="anchor"
  LinkedObject = -> Body005
FEATURE [App::FeaturePython] GroundedJoint  # Assembly grounded joint (typed FeaturePython)
  ObjectToGround = -> Shaft
FEATURE [Assembly::JointGroup] Joints
  Group = -> [GroundedJoint]
FEATURE [App::Link] Shaft001
  LinkedObject = -> Body005
  expr: .Placement.Rotation.Angle = <<MotorSpreadsheet>>.Angle
FEATURE [App::Link] NorthMagnet  label="NorthMagnet001"
  LinkPlacement = pos=(0.00629139,-23.032,0.208473) rot=(0,0,1;0rad)
  LinkedObject = -> Body001
  Placement = pos=(0.00629139,-23.032,0.208473) rot=(0,0,1;0rad)
FEATURE [App::Link] SouthMagnet  label="SouthMagnet001"
  LinkPlacement = pos=(0,-23,0) rot=(0,1,0;3.14159rad)
  LinkedObject = -> Body003
  Placement = pos=(0,-23,0) rot=(0,1,0;3.14159rad)
FEATURE [App::Link] RotorSupport  label="RotorSupport001"
  LinkPlacement = pos=(0,-23,0) rot=(0,1,0;0rad)
  LinkedObject = -> Body008
  Placement = pos=(0,-23,0) rot=(0,1,0;0rad)
  expr: .Placement.Rotation.Angle = <<MotorSpreadsheet>>.Angle
FEATURE [App::Link] Rotor  label="Rotor001"
  LinkPlacement = pos=(0,-14,0) rot=(0,1,0;0rad)
  LinkedObject = -> Body004
  Placement = pos=(0,-14,0) rot=(0,1,0;0rad)
  expr: .Placement.Rotation.Angle = <<MotorSpreadsheet>>.Angle
FEATURE [App::Link] Commutator  label="Commutator001"
  LinkPlacement = pos=(0,-2,0) rot=(0,1,0;0.785398rad)
  LinkedObject = -> Body
  Placement = pos=(0,-2,0) rot=(0,1,0;0.785398rad)
  expr: .Placement.Rotation.Angle = <<MotorSpreadsheet>>.Angle + 45
FEATURE [App::Link] CommutatorSupport  label="CommutatorSupport001"
  LinkPlacement = pos=(0,-2,0) rot=(0,1,0;0rad)
  LinkedObject = -> Body007
  Placement = pos=(0,-2,0) rot=(0,1,0;0rad)
  expr: .Placement.Rotation.Angle = <<MotorSpreadsheet>>.Angle
FEATURE [App::Link] Brush  label="Brush001"
  LinkPlacement = pos=(4.76837e-07,-2.00001,-5.68e-14) rot=(0,0,1;0rad)
  LinkedObject = -> Body002
  Placement = pos=(4.76837e-07,-2.00001,-5.68e-14) rot=(0,0,1;0rad)
FEATURE [App::Link] Brush001  label="Brush002"
  LinkPlacement = pos=(0,-2,0.32) rot=(0,1,0;3.14159rad)
  LinkedObject = -> Body002
  Placement = pos=(0,-2,0.32) rot=(0,1,0;3.14159rad)
FEATURE [App::Link] BrushArms  label="BrushArms001"
  LinkPlacement = pos=(-0.0749995,-17,-0.5) rot=(0,0,1;0rad)
  LinkedObject = -> Body006
  Placement = pos=(-0.0749995,-17,-0.5) rot=(0,0,1;0rad)
FEATURE [App::Link] BrushArms001  label="BrushArms002"
  LinkPlacement = pos=(0.075,-17,0.82) rot=(0,-1,0;3.14159rad)
  LinkedObject = -> Body006
  Placement = pos=(0.075,-17,0.82) rot=(0,-1,0;3.14159rad)
FEATURE [App::Link] Rotor001  label="Rotor002"
  LinkPlacement = pos=(0,-14,0) rot=(0,1,0;1.5708rad)
  LinkedObject = -> Body004
  Placement = pos=(0,-14,0) rot=(0,1,0;1.5708rad)
  expr: .Placement.Rotation.Angle = <<MotorSpreadsheet>>.Angle + 90
FEATURE [App::Link] Case  label="Case001"
  LinkPlacement = pos=(0,10,0) rot=(0,0,1;0rad)
  LinkedObject = -> Body009
  Placement = pos=(0,10,0) rot=(0,0,1;0rad)
FEATURE [App::Link] Case001  label="Case002"
  LinkPlacement = pos=(0,10,0) rot=(0,1,0;3.14159rad)
  LinkedObject = -> Body009
  Placement = pos=(0,10,0) rot=(0,1,0;3.14159rad)
FEATURE [Assembly::AssemblyObject] Assembly
  Group = -> [Joints,Shaft,GroundedJoint,Shaft001,NorthMagnet,SouthMagnet,RotorSupport,Rotor,Commutator,CommutatorSupport,Brush,Brush001,BrushArms,BrushArms001,Rotor001,Case,Case001]
  Origin = -> Origin011
  Type = Assembly
